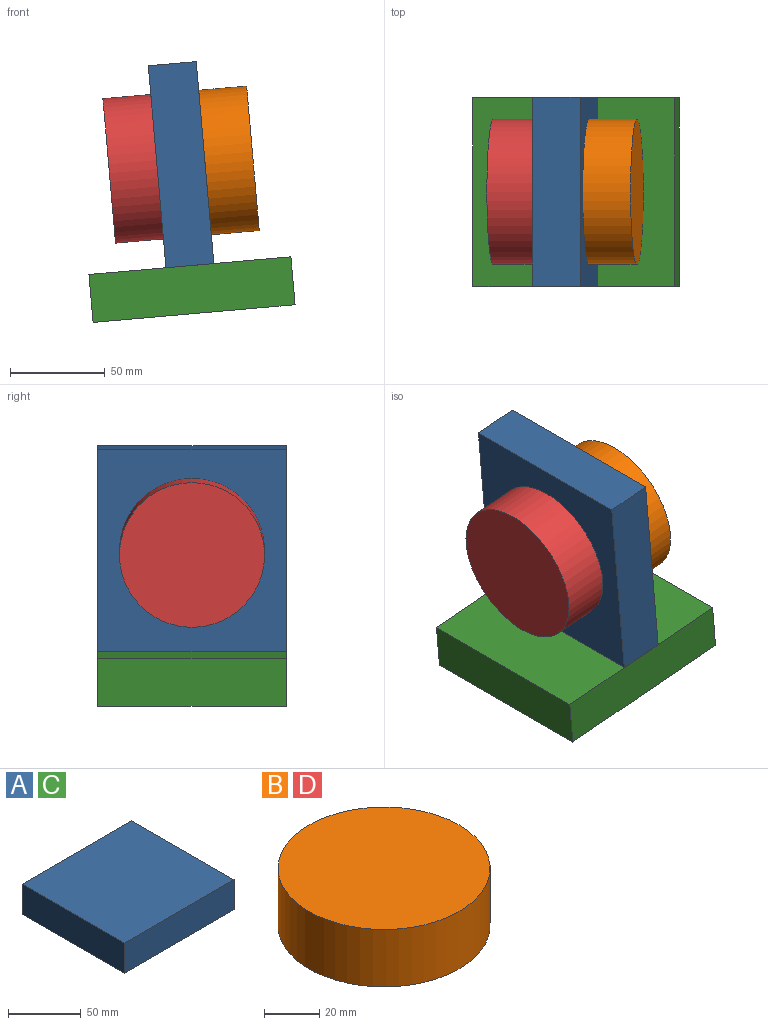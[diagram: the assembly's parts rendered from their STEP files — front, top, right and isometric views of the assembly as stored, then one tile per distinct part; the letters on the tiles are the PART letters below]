
ASSEMBLY  parts=4 mates=3
PART A: 6 faces, bbox 107.1x99.6x25.4 mm
  f0: plane 99.61x25.4mm, normal (1,0,0), area 2530.2mm2, adj f1,f3,f4,f5
  f1: plane 107.09x25.4mm, normal (0,1,0), area 2720.1mm2, adj f0,f2,f4,f5
  f2: plane 99.61x25.4mm, normal (-1,0,0), area 2530.2mm2, adj f1,f3,f4,f5
  f3: plane 107.09x25.4mm, normal (0,-1,0), area 2720.1mm2, adj f0,f2,f4,f5
  f4: plane 107.09x99.61mm, normal (0,0,1), area 10667.7mm2, adj f0,f1,f2,f3
  f5: plane 107.09x99.61mm, normal (0,0,-1), area 10667.7mm2, adj f0,f1,f2,f3
PART B: 3 faces, bbox 76.7x76.7x25.4 mm
  f0: cylinder r=38.33mm len=76.65mm, axis (0,0,-1), area 6116.7mm2, adj f1,f2
  f1: plane 76.65x76.65mm, normal (0,0,1), area 4614.9mm2, adj f0
  f2: plane 76.65x76.65mm, normal (0,0,-1), area 4614.9mm2, adj f0
PART C: same geometry as A
PART D: same geometry as B
PLACE A rot(axis=(0,-1,0),95deg) t=(261.41,236.08,102.71)mm
PLACE B rot(axis=(0,-1,0),95deg) t=(286.44,242.87,108.08)mm
PLACE C rot(axis=(0,-1,0),5deg) t=(252.21,236.08,25.83)mm fixed
PLACE D rot(axis=(0,-1,0),95deg) t=(235.83,242.87,103.65)mm
MATE fastened B.f0 <-> A.f5  axis (-1,0,-0.09) through (261.13,242.87,105.86)mm
MATE fastened D.f0 <-> A.f4  axis (1,0,0.09) through (235.83,242.87,103.65)mm
MATE fastened C.f4 <-> A.f2  axis (-0.09,0,1) through (253.15,242.87,51.41)mm
